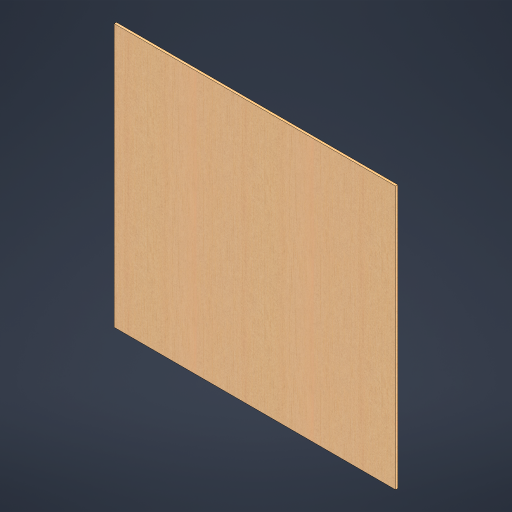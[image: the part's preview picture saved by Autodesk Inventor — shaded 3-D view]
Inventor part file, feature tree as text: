
AUTODESK INVENTOR PART (.ipt)
format: ipt  version: 2024 (Build 280153000, 153)  size: 320,512 bytes
history: native  units: mm
features: other x2, extrude x1, sketch x1
ambient origin geometry x8: Origin, YZ Plane, XZ Plane, XY Plane, X Axis, Y Axis, Z Axis, Center Point
bodies: Body1 (feature_tree)
feature tree (4):
  other  "솔리드1"
  extrude  "돌출1"  Depth=610.0mm
  sketch  "스케치1"
  other  "Finish1"
